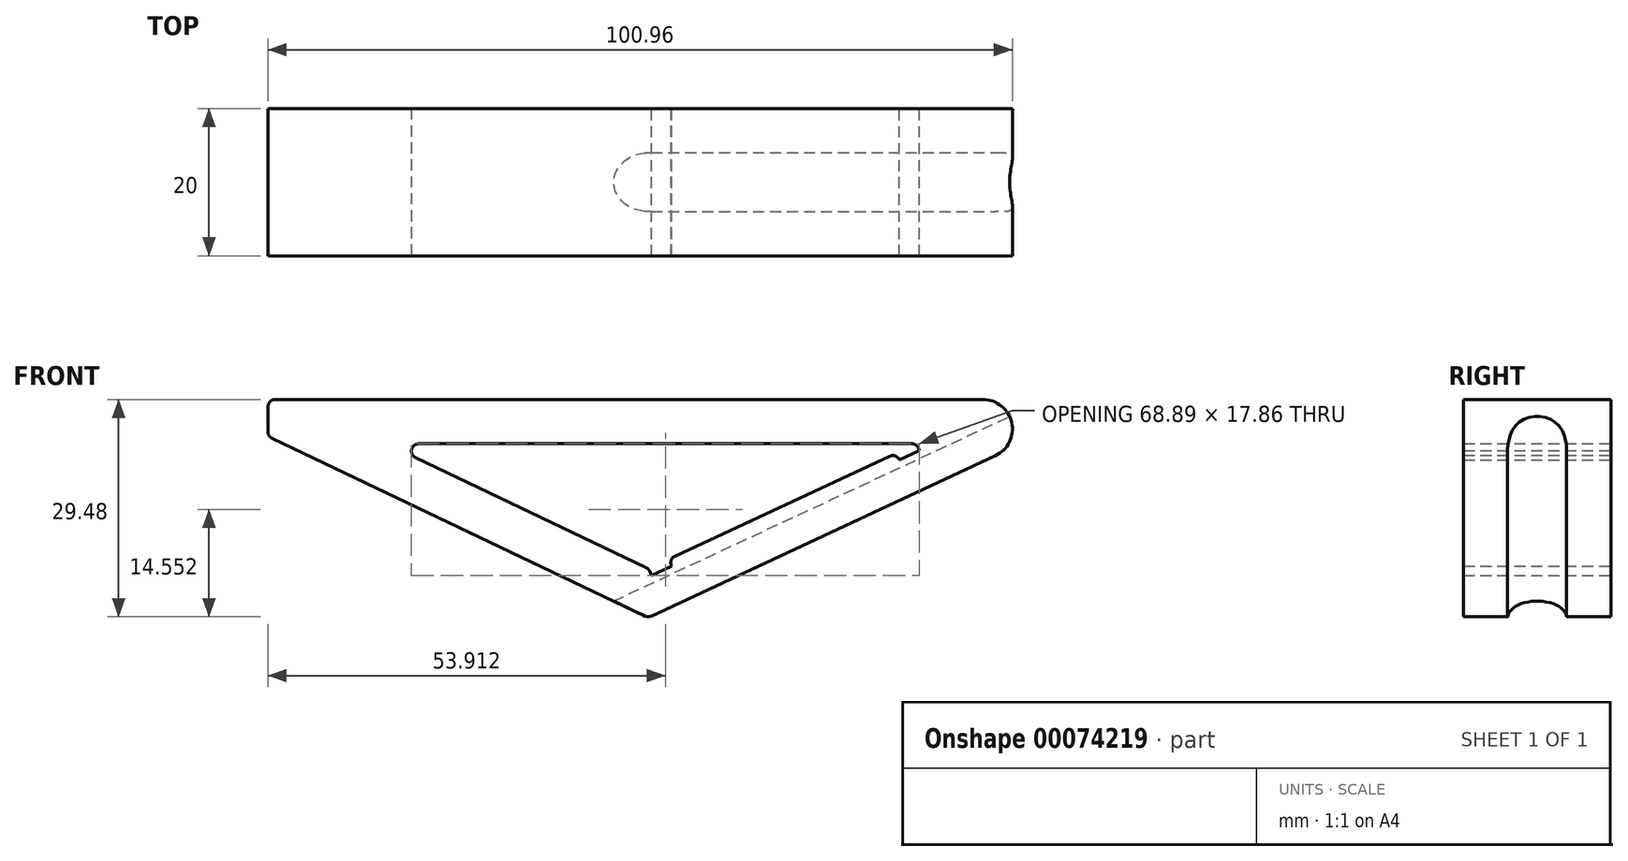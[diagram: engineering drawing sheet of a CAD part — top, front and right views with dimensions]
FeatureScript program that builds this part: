
annotation { "Feature Type Name" : "Feature", "Feature Type Description" : "" }
export const myFeature = defineFeature(function(context is Context, id is Id, definition is map)
    precondition{}
    {
        {
            var Q0;
            Q0=qCreatedBy(makeId("Front.planeOp"),FACE);
            var sketch = newSketch(context, id + "F0", { "sketchPlane" : qUnion([Q0])});
            skLineSegment(sketch, "E0", {"start": v(0, 0) * mm, "end": v(-63.44, -29.58) * mm});
            skLineSegment(sketch, "E1", {"start": v(-63.44, -29.58) * mm, "end": v(-115, -5) * mm});
            skLineSegment(sketch, "E2", {"start": v(-115, 0) * mm, "end": v(0, 0) * mm});
            skLineSegment(sketch, "E3", {"start": v(-115, 0) * mm, "end": v(-115, -5) * mm});
            skSolve(sketch);
        }
        {
            var Q0;
            Q0 = qSketchRegion(id + "F0", true);
            extrude(context, id + "F1", {"entities" : qUnion([Q0]), "depth" : 50 * mm});
        }
        {
            var Q0;
            Q0=makeQuery(id+"F1.opExtrude","SWEPT_EDGE",EDGE,{"disambiguationData":[OSD([sQuery(id+"F0.wireOp",EDGE,"E0"),sQuery(id+"F0.wireOp",EDGE,"E2")])]});
            cPlane(context, id + "F2", {"entities" : qUnion([Q0]), "cplaneType" : CPlaneType.LINE_ANGLE, "offset" : 150 * mm, "angle" : 65 * degree, "width" : 150 * mm, "height" : 150 * mm});
        }
        {
            var Q0;
            Q0=makeQuery(id+"F1.opExtrude","SWEPT_EDGE",EDGE,{"disambiguationData":[OSD([sQuery(id+"F0.wireOp",EDGE,"E0"),sQuery(id+"F0.wireOp",EDGE,"E1")])]});
            var Q1;
            Q1=makeQuery(id+"F1.opExtrude","SWEPT_EDGE",EDGE,{"disambiguationData":[OSD([sQuery(id+"F0.wireOp",EDGE,"E1"),sQuery(id+"F0.wireOp",EDGE,"E3")])]});
            var Q2;
            Q2=makeQuery(id+"F1.opExtrude","SWEPT_EDGE",EDGE,{"disambiguationData":[OSD([sQuery(id+"F0.wireOp",EDGE,"E2"),sQuery(id+"F0.wireOp",EDGE,"E3")])]});
            fillet(context, id + "F3", {"entities" : qUnion([Q0, Q1, Q2]), "radius" : 1 * mm, "tangentPropagation" : true, "allowEdgeOverflow" : false});
        }
        {
            var Q0;
            Q0=makeQuery(id+"F1.opExtrude","SWEPT_EDGE",EDGE,{"disambiguationData":[OSD([sQuery(id+"F0.wireOp",EDGE,"E0"),sQuery(id+"F0.wireOp",EDGE,"E2")])]});
            fillet(context, id + "F4", {"entities" : qUnion([Q0]), "radius" : 4 * mm, "tangentPropagation" : true, "allowEdgeOverflow" : false});
        }
        {
            var Q0;
            Q0=qCreatedBy(id+"F2.planeOp",FACE);
            var sketch = newSketch(context, id + "F5", { "sketchPlane" : qUnion([Q0])});
            skCircle(sketch, "E4", {"center": v(-40, 0) * mm, "radius": 4 * mm});
            skSolve(sketch);
        }
        {
            var Q0;
            Q0 = qSketchRegion(id + "F5", true);
            extrude(context, id + "F6", {"entities" : qUnion([Q0]), "operationType" : NewBodyOperationType.REMOVE, "endBound" : BoundingType.THROUGH_ALL, "oppositeDirection" : true, "depth" : 25 * mm});
        }
        {
            var Q0;
            Q0=qCreatedBy(makeId("Front.planeOp"),FACE);
            var sketch = newSketch(context, id + "F7", { "sketchPlane" : qUnion([Q0])});
            skLineSegment(sketch, "E5.0", {"start": v(-98.96, -6) * mm, "end": v(-27.06, -6) * mm});
            skLineSegment(sketch, "E5.1", {"start": v(-63.41, -22.95) * mm, "end": v(-98.96, -6) * mm});
            skLineSegment(sketch, "E5.2", {"start": v(-29.78, -7.27) * mm, "end": v(-60.7, -21.68) * mm});
            skLineSegment(sketch, "E6", {"start": v(-63.41, -22.95) * mm, "end": v(-63, -23.86) * mm});
            skLineSegment(sketch, "E7", {"start": v(-63, -23.86) * mm, "end": v(-60.27, -22.59) * mm});
            skLineSegment(sketch, "E8", {"start": v(-60.27, -22.59) * mm, "end": v(-60.7, -21.68) * mm});
            skLineSegment(sketch, "E9", {"start": v(-27.06, -6) * mm, "end": v(-26.64, -6.9) * mm});
            skLineSegment(sketch, "E10", {"start": v(-26.64, -6.9) * mm, "end": v(-29.36, -8.17) * mm});
            skLineSegment(sketch, "E11", {"start": v(-29.36, -8.17) * mm, "end": v(-29.78, -7.27) * mm});
            skSolve(sketch);
        }
        {
            var Q0;
            Q0 = qSketchRegion(id + "F7", true);
            extrude(context, id + "F8", {"entities" : qUnion([Q0]), "operationType" : NewBodyOperationType.REMOVE, "endBound" : BoundingType.THROUGH_ALL, "depth" : 25 * mm});
        }
        {
            var Q0;
            Q0=makeQuery(id+"F8.boolean.opBoolean","COPY",EDGE,{"derivedFrom":makeQuery(id+"F8.opExtrude","SWEPT_EDGE",EDGE,{"disambiguationData":[OSD([sQuery(id+"F7.wireOp",EDGE,"E5.0"),sQuery(id+"F7.wireOp",EDGE,"E5.1")])]})});
            var Q1;
            Q1=makeQuery(id+"F8.boolean.opBoolean","COPY",EDGE,{"derivedFrom":makeQuery(id+"F8.opExtrude","SWEPT_EDGE",EDGE,{"disambiguationData":[OSD([sQuery(id+"F7.wireOp",EDGE,"E5.2"),sQuery(id+"F7.wireOp",EDGE,"E8")])]})});
            var Q2;
            Q2=makeQuery(id+"F8.boolean.opBoolean","COPY",EDGE,{"derivedFrom":makeQuery(id+"F8.opExtrude","SWEPT_EDGE",EDGE,{"disambiguationData":[OSD([sQuery(id+"F7.wireOp",EDGE,"E5.2"),sQuery(id+"F7.wireOp",EDGE,"E11")])]})});
            var Q3;
            Q3=makeQuery(id+"F8.boolean.opBoolean","COPY",EDGE,{"derivedFrom":makeQuery(id+"F8.opExtrude","SWEPT_EDGE",EDGE,{"disambiguationData":[OSD([sQuery(id+"F7.wireOp",EDGE,"E5.0"),sQuery(id+"F7.wireOp",EDGE,"E9")])]})});
            var Q4;
            Q4=makeQuery(id+"F8.boolean.opBoolean","COPY",EDGE,{"derivedFrom":makeQuery(id+"F8.opExtrude","SWEPT_EDGE",EDGE,{"disambiguationData":[OSD([sQuery(id+"F7.wireOp",EDGE,"E5.1"),sQuery(id+"F7.wireOp",EDGE,"E6")])]})});
            fillet(context, id + "F9", {"entities" : qUnion([Q0, Q1, Q2, Q3, Q4]), "radius" : 1 * mm, "tangentPropagation" : true, "allowEdgeOverflow" : false});
        }
        {
            var Q0;
            Q0 = qSketchRegion(id + "F0", true);
            extrude(context, id + "F10", {"entities" : qUnion([Q0]), "operationType" : NewBodyOperationType.REMOVE, "depth" : 30 * mm});
        }
    });
